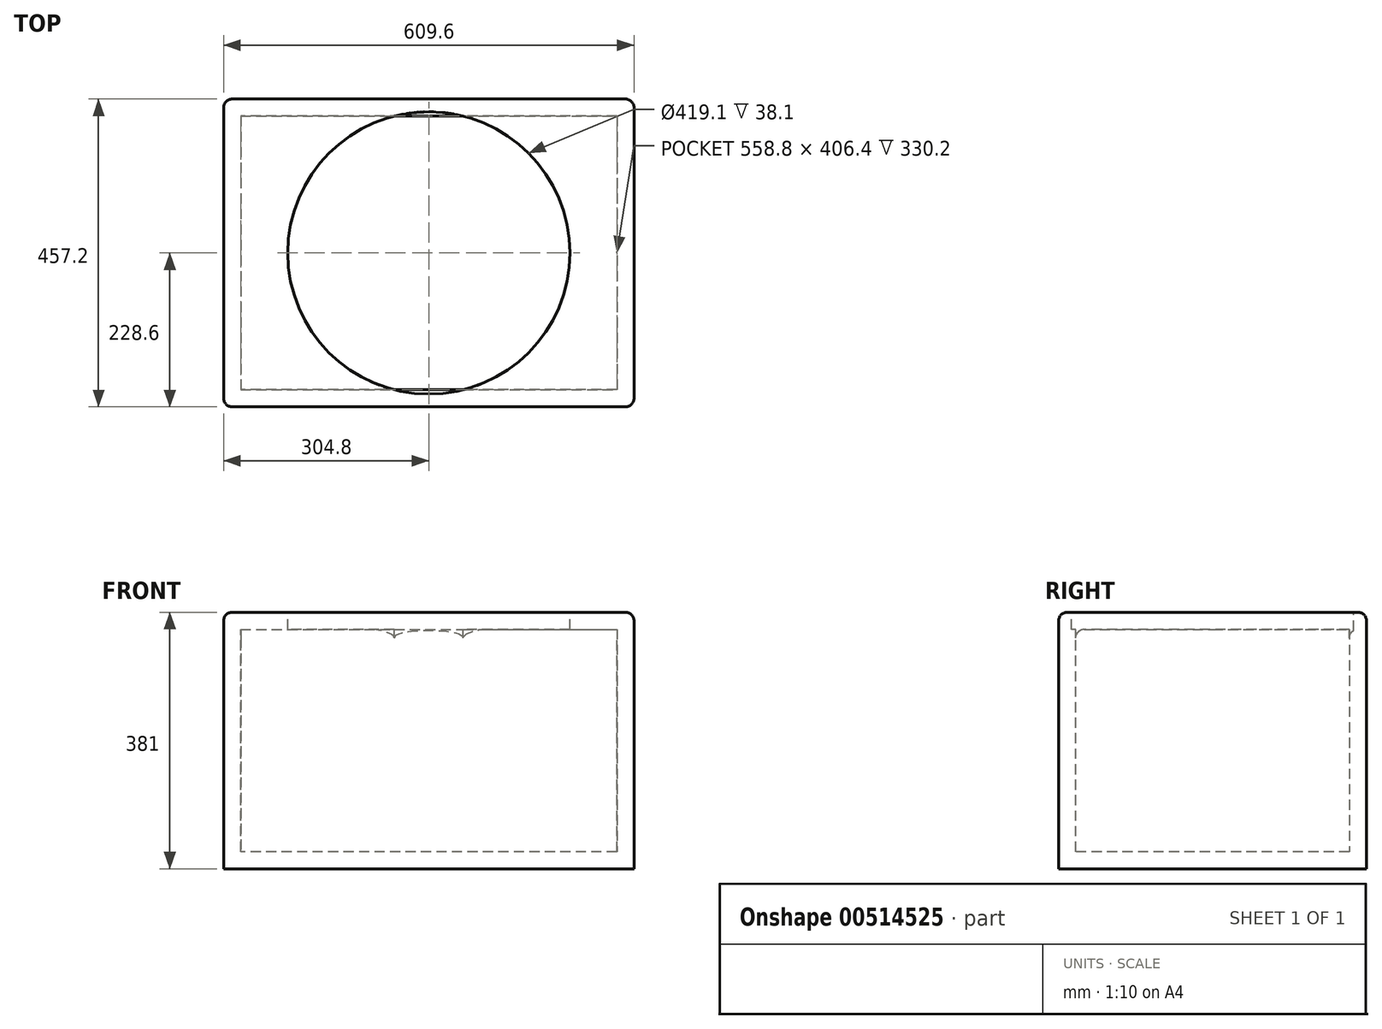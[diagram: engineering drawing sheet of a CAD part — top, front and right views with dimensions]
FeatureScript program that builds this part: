
annotation { "Feature Type Name" : "Feature", "Feature Type Description" : "" }
export const myFeature = defineFeature(function(context is Context, id is Id, definition is map)
    precondition{}
    {
        {
            var Q0;
            Q0=qCreatedBy(makeId("Top.planeOp"),FACE);
            var sketch = newSketch(context, id + "F0", { "sketchPlane" : qUnion([Q0])});
            skLineSegment(sketch, "E0.bottom", {"start": v(304.8, 228.6) * mm, "end": v(-304.8, 228.6) * mm});
            skLineSegment(sketch, "E0.top", {"start": v(304.8, -228.6) * mm, "end": v(-304.8, -228.6) * mm});
            skLineSegment(sketch, "E0.left", {"start": v(304.8, 228.6) * mm, "end": v(304.8, -228.6) * mm});
            skLineSegment(sketch, "E0.right", {"start": v(-304.8, 228.6) * mm, "end": v(-304.8, -228.6) * mm});
            skPoint(sketch, "E0.middle", {"position": v(0, 0) * mm});
            skSolve(sketch);
        }
        {
            var Q0;
            Q0=makeQuery(id+"F0.imprint","IMPRINT",FACE,{"disambiguationData":[TD([[makeQuery(id+"F0.imprint","IMPRINT",EDGE,{"derivedFrom":sQuery(id+"F0.wireOp",EDGE,"E0.bottom")}),1.0]])]});
            extrude(context, id + "F1", {"entities" : qUnion([Q0]), "depth" : 381 * mm, "offsetDistance" : 25.4 * mm});
        }
        {
            var Q0;
            Q0=makeQuery(id+"F1.opExtrude","CAP_FACE",FACE,{"disambiguationData":[OSD([sQuery(id+"F0.wireOp",EDGE,"E0.bottom"),sQuery(id+"F0.wireOp",EDGE,"E0.top"),sQuery(id+"F0.wireOp",EDGE,"E0.left"),sQuery(id+"F0.wireOp",EDGE,"E0.right")])],"isStart":false});
            var Q1;
            Q1=makeQuery(id+"F1.opExtrude","SWEPT_EDGE",EDGE,{"disambiguationData":[OSD([sQuery(id+"F0.wireOp",EDGE,"E0.top"),sQuery(id+"F0.wireOp",EDGE,"E0.right")])]});
            var Q2;
            Q2=makeQuery(id+"F1.opExtrude","SWEPT_EDGE",EDGE,{"disambiguationData":[OSD([sQuery(id+"F0.wireOp",EDGE,"E0.top"),sQuery(id+"F0.wireOp",EDGE,"E0.left")])]});
            var Q3;
            Q3=makeQuery(id+"F1.opExtrude","SWEPT_EDGE",EDGE,{"disambiguationData":[OSD([sQuery(id+"F0.wireOp",EDGE,"E0.bottom"),sQuery(id+"F0.wireOp",EDGE,"E0.left")])]});
            var Q4;
            Q4=makeQuery(id+"F1.opExtrude","SWEPT_EDGE",EDGE,{"disambiguationData":[OSD([sQuery(id+"F0.wireOp",EDGE,"E0.bottom"),sQuery(id+"F0.wireOp",EDGE,"E0.right")])]});
            fillet(context, id + "F2", {"entities" : qUnion([Q0, Q1, Q2, Q3, Q4]), "radius" : 12.7 * mm, "tangentPropagation" : true, "allowEdgeOverflow" : false});
        }
        {
            var Q0;
            Q0=makeQuery(id+"F1.opExtrude","CAP_FACE",FACE,{"disambiguationData":[OSD([sQuery(id+"F0.wireOp",EDGE,"E0.bottom"),sQuery(id+"F0.wireOp",EDGE,"E0.top"),sQuery(id+"F0.wireOp",EDGE,"E0.left"),sQuery(id+"F0.wireOp",EDGE,"E0.right")])],"isStart":false});
            var Q1;
            Q1=makeQuery(id+"F1.opExtrude","SWEPT_BODY",BODY,{"disambiguationData":[OSD([sQuery(id+"F0.wireOp",EDGE,"E0.bottom"),sQuery(id+"F0.wireOp",EDGE,"E0.top"),sQuery(id+"F0.wireOp",EDGE,"E0.left"),sQuery(id+"F0.wireOp",EDGE,"E0.right")])]});
            shell(context, id + "F3", {"isHollow" : true, "entities" : qUnion([Q0]), "parts" : qUnion([Q1]), "thickness" : 25.4 * mm});
        }
        {
            var Q0;
            Q0=makeQuery(id+"F1.opExtrude","CAP_FACE",FACE,{"disambiguationData":[OSD([sQuery(id+"F0.wireOp",EDGE,"E0.bottom"),sQuery(id+"F0.wireOp",EDGE,"E0.top"),sQuery(id+"F0.wireOp",EDGE,"E0.left"),sQuery(id+"F0.wireOp",EDGE,"E0.right")])],"isStart":false});
            var sketch = newSketch(context, id + "F4", { "sketchPlane" : qUnion([Q0])});
            skCircle(sketch, "E1", {"center": v(0, 0) * mm, "radius": 209.55 * mm});
            skSolve(sketch);
        }
        {
            var Q0;
            Q0=makeQuery(id+"F4.imprint","IMPRINT",FACE,{"disambiguationData":[TD([[makeQuery(id+"F4.imprint","IMPRINT",EDGE,{"derivedFrom":sQuery(id+"F4.wireOp",EDGE,"E1")}),1.0]])]});
            extrude(context, id + "F5", {"entities" : qUnion([Q0]), "operationType" : NewBodyOperationType.REMOVE, "oppositeDirection" : true, "depth" : 25.4 * mm, "offsetDistance" : 25.4 * mm});
        }
        {
            var Q0;
            {var subQ0=sQuery(id+"F0.wireOp",EDGE,"E0.bottom");var subQ1=sQuery(id+"F0.wireOp",EDGE,"E0.right");var subQ2=sQuery(id+"F0.wireOp",EDGE,"E0.left");var subQ3=sQuery(id+"F0.wireOp",EDGE,"E0.top");var subQ4=makeQuery(id+"F1.opExtrude","CAP_EDGE",EDGE,{"disambiguationData":[OSD([subQ0])],"isStart":false});Q0=makeQuery(id+"F5.boolean.opBoolean","SPLIT",EDGE,{"disambiguationData":[topologyDisambiguationEdgeConnected([makeQuery(id+"F3.opShell","OFFSET_FACE",FACE,{"disambiguationData":[OSD([subQ0])]}),makeQuery(id+"F5.opExtrude","CAP_FACE",FACE,{"disambiguationData":[OSD([sQuery(id+"F4.wireOp",EDGE,"E1")])],"isStart":false})])],"derivedFrom":makeQuery(id+"F3.opShell","OFFSET_EDGE",EDGE,{"disambiguationData":[OSD([subQ0,subQ3,subQ2,subQ1]),TDD([makeQuery(id+"F2.opFillet","BLEND_EDGE",EDGE,{"blendedFrom":[subQ4,makeQuery(id+"F1.opExtrude","SWEPT_FACE",FACE,{"disambiguationData":[OSD([subQ0])]})],"blendedInto":[makeQuery(id+"F1.opExtrude","SWEPT_FACE",FACE,{"disambiguationData":[OSD([subQ0])]})]}),makeQuery(id+"F2.opFillet","BLEND_EDGE",EDGE,{"blendedFrom":[subQ4,makeQuery(id+"F1.opExtrude","CAP_FACE",FACE,{"disambiguationData":[OSD([subQ0,subQ3,subQ2,subQ1])],"isStart":false})],"blendedInto":[makeQuery(id+"F1.opExtrude","CAP_FACE",FACE,{"disambiguationData":[OSD([subQ0,subQ3,subQ2,subQ1])],"isStart":false})]})])]})});}
            var Q1;
            {var subQ0=sQuery(id+"F0.wireOp",EDGE,"E0.top");var subQ1=makeQuery(id+"F1.opExtrude","CAP_EDGE",EDGE,{"disambiguationData":[OSD([subQ0])],"isStart":false});var subQ2=sQuery(id+"F0.wireOp",EDGE,"E0.right");var subQ3=sQuery(id+"F0.wireOp",EDGE,"E0.left");var subQ4=sQuery(id+"F0.wireOp",EDGE,"E0.bottom");Q1=makeQuery(id+"F5.boolean.opBoolean","SPLIT",EDGE,{"disambiguationData":[topologyDisambiguationEdgeConnected([makeQuery(id+"F3.opShell","OFFSET_FACE",FACE,{"disambiguationData":[OSD([subQ0])]}),makeQuery(id+"F5.opExtrude","CAP_FACE",FACE,{"disambiguationData":[OSD([sQuery(id+"F4.wireOp",EDGE,"E1")])],"isStart":false})])],"derivedFrom":makeQuery(id+"F3.opShell","OFFSET_EDGE",EDGE,{"disambiguationData":[OSD([subQ4,subQ0,subQ3,subQ2]),TDD([makeQuery(id+"F2.opFillet","BLEND_EDGE",EDGE,{"blendedFrom":[subQ1,makeQuery(id+"F1.opExtrude","CAP_FACE",FACE,{"disambiguationData":[OSD([subQ4,subQ0,subQ3,subQ2])],"isStart":false})],"blendedInto":[makeQuery(id+"F1.opExtrude","CAP_FACE",FACE,{"disambiguationData":[OSD([subQ4,subQ0,subQ3,subQ2])],"isStart":false})]}),makeQuery(id+"F2.opFillet","BLEND_EDGE",EDGE,{"blendedFrom":[subQ1,makeQuery(id+"F1.opExtrude","SWEPT_FACE",FACE,{"disambiguationData":[OSD([subQ0])]})],"blendedInto":[makeQuery(id+"F1.opExtrude","SWEPT_FACE",FACE,{"disambiguationData":[OSD([subQ0])]})]})])]})});}
            fillet(context, id + "F6", {"entities" : qUnion([Q0, Q1]), "radius" : 12.7 * mm, "tangentPropagation" : true, "allowEdgeOverflow" : false});
        }
    });
